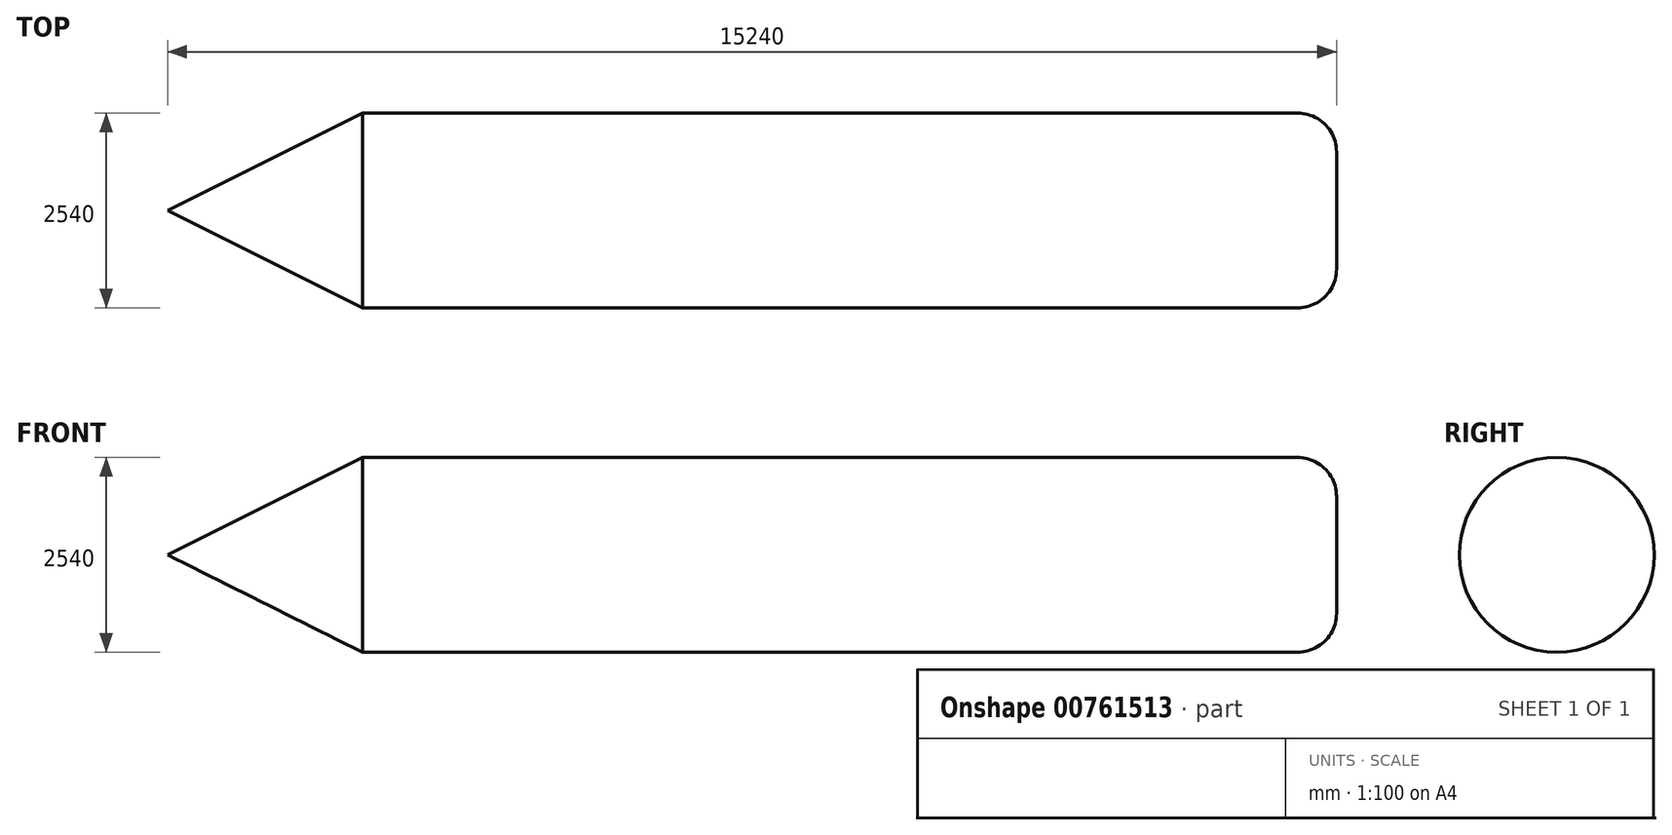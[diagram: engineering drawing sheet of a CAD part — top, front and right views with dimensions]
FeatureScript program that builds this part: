
annotation { "Feature Type Name" : "Feature", "Feature Type Description" : "" }
export const myFeature = defineFeature(function(context is Context, id is Id, definition is map)
    precondition{}
    {
        {
            var Q0;
            Q0=qCreatedBy(makeId("Right.planeOp"),FACE);
            var sketch = newSketch(context, id + "F0", { "sketchPlane" : qUnion([Q0])});
            skCircle(sketch, "E0", {"center": v(0, 0) * mm, "radius": 1270 * mm});
            skSolve(sketch);
        }
        {
            var Q0;
            Q0=makeQuery(id+"F0.imprint","IMPRINT",FACE,{"disambiguationData":[TD([[makeQuery(id+"F0.imprint","IMPRINT",EDGE,{"derivedFrom":sQuery(id+"F0.wireOp",EDGE,"E0")}),1.0]])]});
            extrude(context, id + "F1", {"entities" : qUnion([Q0]), "endBound" : BoundingType.SYMMETRIC, "depth" : 12700 * mm, "offsetDistance" : 25.4 * mm});
        }
        {
            var Q0;
            Q0=makeQuery(id+"F1.opExtrude","CAP_EDGE",EDGE,{"disambiguationData":[OSD([sQuery(id+"F0.wireOp",EDGE,"E0")])],"isStart":false});
            fillet(context, id + "F2", {"entities" : qUnion([Q0]), "radius" : 508 * mm, "tangentPropagation" : true, "allowEdgeOverflow" : false});
        }
        {
            var Q0;
            Q0=qCreatedBy(makeId("Front.planeOp"),FACE);
            var sketch = newSketch(context, id + "F3", { "sketchPlane" : qUnion([Q0])});
            skLineSegment(sketch, "E1", {"start": v(-6350, 1270) * mm, "end": v(-6350, 0) * mm});
            skLineSegment(sketch, "E2", {"start": v(-8890, 0) * mm, "end": v(-6350, 1270) * mm});
            skLineSegment(sketch, "E3", {"start": v(-8890, 0) * mm, "end": v(-6350, 0) * mm});
            skSolve(sketch);
        }
        {
            var Q0;
            Q0=makeQuery(id+"F3.imprint","IMPRINT",FACE,{"disambiguationData":[TD([[makeQuery(id+"F3.imprint","IMPRINT",EDGE,{"derivedFrom":sQuery(id+"F3.wireOp",EDGE,"E1")}),-1.0]])]});
            var Q1;
            Q1=sQuery(id+"F3.wireOp",EDGE,"E3");
            revolve(context, id + "F4", {"operationType" : NewBodyOperationType.ADD, "surfaceOperationType" : NewSurfaceOperationType.NEW, "entities" : qUnion([Q0]), "axis" : qUnion([Q1]), "revolveType" : RevolveType.FULL});
        }
    });
